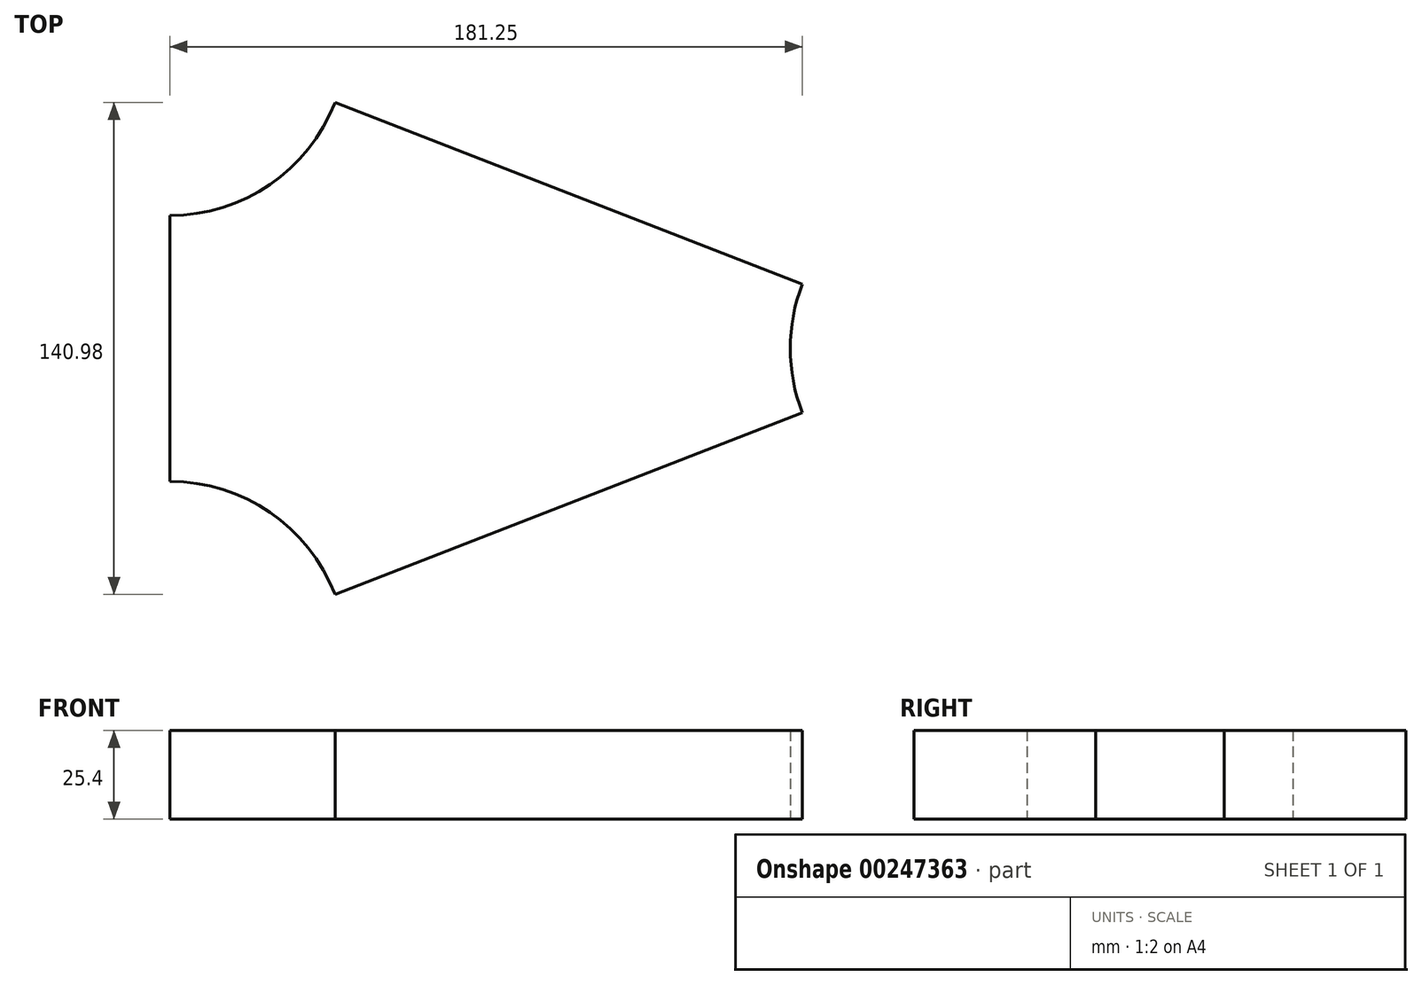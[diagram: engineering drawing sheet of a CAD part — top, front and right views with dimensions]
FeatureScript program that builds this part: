
annotation { "Feature Type Name" : "Feature", "Feature Type Description" : "" }
export const myFeature = defineFeature(function(context is Context, id is Id, definition is map)
    precondition{}
    {
        {
            var Q0;
            Q0=qCreatedBy(makeId("Top.planeOp"),FACE);
            var sketch = newSketch(context, id + "F0", { "sketchPlane" : qUnion([Q0])});
            skLineSegment(sketch, "E0", {"start": v(-91.44, 0) * mm, "end": v(137.16, 0) * mm});
            skLineSegment(sketch, "E1", {"start": v(-91.44, 0) * mm, "end": v(-91.44, 38.1) * mm});
            skLineSegment(sketch, "E2.MirrorCS", {"start": v(-91.44, 0) * mm, "end": v(-91.44, -38.1) * mm});
            skLineSegment(sketch, "E3", {"start": v(-44.1, -70.49) * mm, "end": v(89.81, -18.41) * mm});
            skLineSegment(sketch, "E4", {"start": v(-44.1, 70.49) * mm, "end": v(89.81, 18.41) * mm});
            skArc(sketch, "E5", {"start": v(89.81, 18.41) * mm, "mid": v(86.36, 0) * mm, "end": v(89.81, -18.41) * mm});
            skArc(sketch, "E6", {"start": v(-91.44, 38.1) * mm, "mid": v(-62.76, 46.97) * mm, "end": v(-44.1, 70.49) * mm});
            skArc(sketch, "E7", {"start": v(-44.1, -70.49) * mm, "mid": v(-62.76, -46.97) * mm, "end": v(-91.44, -38.1) * mm});
            skSolve(sketch);
        }
        {
            var Q0;
            Q0 = qSketchRegion(id + "F0", true);
            extrude(context, id + "F1", {"entities" : qUnion([Q0]), "depth" : 25.4 * mm});
        }
    });
